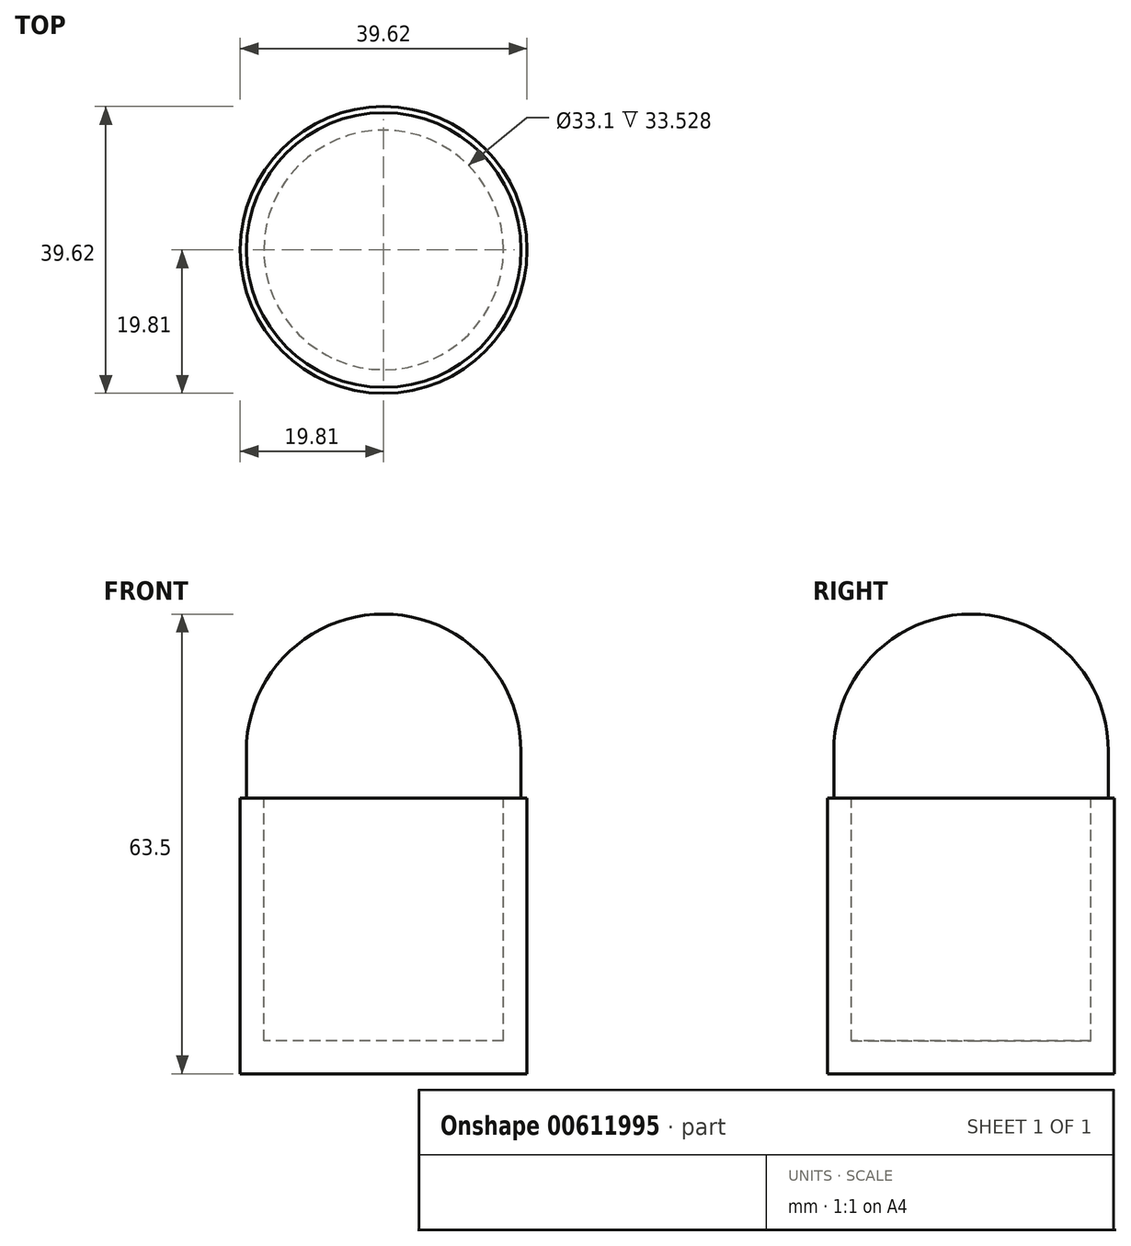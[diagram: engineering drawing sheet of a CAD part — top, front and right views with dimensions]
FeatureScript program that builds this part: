
annotation { "Feature Type Name" : "Feature", "Feature Type Description" : "" }
export const myFeature = defineFeature(function(context is Context, id is Id, definition is map)
    precondition{}
    {
        {
            var Q0;
            Q0=qCreatedBy(makeId("Top.planeOp"),FACE);
            var sketch = newSketch(context, id + "F0", { "sketchPlane" : qUnion([Q0])});
            skCircle(sketch, "E0", {"center": v(0, 0) * mm, "radius": 19.81 * mm});
            skSolve(sketch);
        }
        {
            var Q0;
            Q0=makeQuery(id+"F0.imprint","IMPRINT",FACE,{"disambiguationData":[TD([[makeQuery(id+"F0.imprint","IMPRINT",EDGE,{"derivedFrom":sQuery(id+"F0.wireOp",EDGE,"E0")}),1.0]])]});
            extrude(context, id + "F1", {"entities" : qUnion([Q0]), "depth" : 38.1 * mm, "offsetDistance" : 25.4 * mm});
        }
        {
            var Q0;
            Q0=makeQuery(id+"F1.opExtrude","CAP_FACE",FACE,{"disambiguationData":[OSD([sQuery(id+"F0.wireOp",EDGE,"E0")])],"isStart":false});
            var sketch = newSketch(context, id + "F2", { "sketchPlane" : qUnion([Q0])});
            skCircle(sketch, "E1", {"center": v(0, 0) * mm, "radius": 16.55 * mm});
            skSolve(sketch);
        }
        {
            var Q0;
            Q0 = qSketchRegion(id + "F2", true);
            extrude(context, id + "F3", {"entities" : qUnion([Q0]), "operationType" : NewBodyOperationType.REMOVE, "oppositeDirection" : true, "depth" : 33.53 * mm, "offsetDistance" : 25.4 * mm});
        }
        {
            var Q0;
            Q0=makeQuery(id+"F1.opExtrude","CAP_FACE",FACE,{"disambiguationData":[OSD([sQuery(id+"F0.wireOp",EDGE,"E0")])],"isStart":false});
            var sketch = newSketch(context, id + "F4", { "sketchPlane" : qUnion([Q0])});
            skCircle(sketch, "E2", {"center": v(0, 0) * mm, "radius": 18.97 * mm});
            skSolve(sketch);
        }
        {
            var Q0;
            Q0 = qSketchRegion(id + "F4", true);
            extrude(context, id + "F5", {"entities" : qUnion([Q0]), "operationType" : NewBodyOperationType.ADD, "depth" : 25.4 * mm, "offsetDistance" : 25.4 * mm});
        }
        {
            var Q0;
            Q0=makeQuery(id+"F5.opExtrude","CAP_EDGE",EDGE,{"disambiguationData":[OSD([sQuery(id+"F4.wireOp",EDGE,"E2")])],"isStart":false});
            fillet(context, id + "F6", {"entities" : qUnion([Q0]), "radius" : 18.95 * mm, "tangentPropagation" : true, "allowEdgeOverflow" : false});
        }
    });
